# Revit family: CU2FO
name_source: partatom
category: Lighting Fixtures
units: mm (PartAtom-declared; Revit-internal decimal feet)

## family parameters
Cut with Voids When Loaded = No
Host = Face
Light Source = No
OmniClass Number = 23.80.70.11
OmniClass Title = Luminaries for Internal Lighting
Part Type = Normal
Room Calculation Point = No
Round Connector Dimension = Use Diameter
Shared = No

## types (1)
- CU2FO
    Apparent Load = 2 VA
    Application = Stairwells, Hallways, Offices and other commercial applications
    Backbox = Paint- White
    Certification = UL924 Listed for Damp Location
NFPA 101 and NFPA 70
OSHA
    Default Elevation = 48 "
    Description = LED emergency light with fixed lampheads for consistent and predictable aiming, clear polycarbonate lamp covers, Nickel Cadmium battery
    Features = LED life-cycle of more than 10 years
•	 Quick installation
•	 Dual-voltage 120 or 277V AC input
•	 Includes long-life Nickel Cadmium battery for UL
recognized 90 minute emergency lighting
•	 12 LEDs per lamphead for bright and even illumination
•	 Damp Location Listed 20°C to 30°C (68°F to 86°F)
•	 Provided with test switch and AC-On indicator
•	 Wall or Ceiling mount
    Glass = White Glass
    Lamp = LED Lamp
    Manufacturer = Compass Products
    Model = CU2FO
    Nominal Watts = 2 W
    URL = https://www.currentlighting.com
    Voltage = 120 V
    Warranty = 2Year full unit warranty
    Wattage Comments = 2.4W

## geometry (parser evidence)
native form markers: Sweep x4
no freeform markers — native parametric forms only
